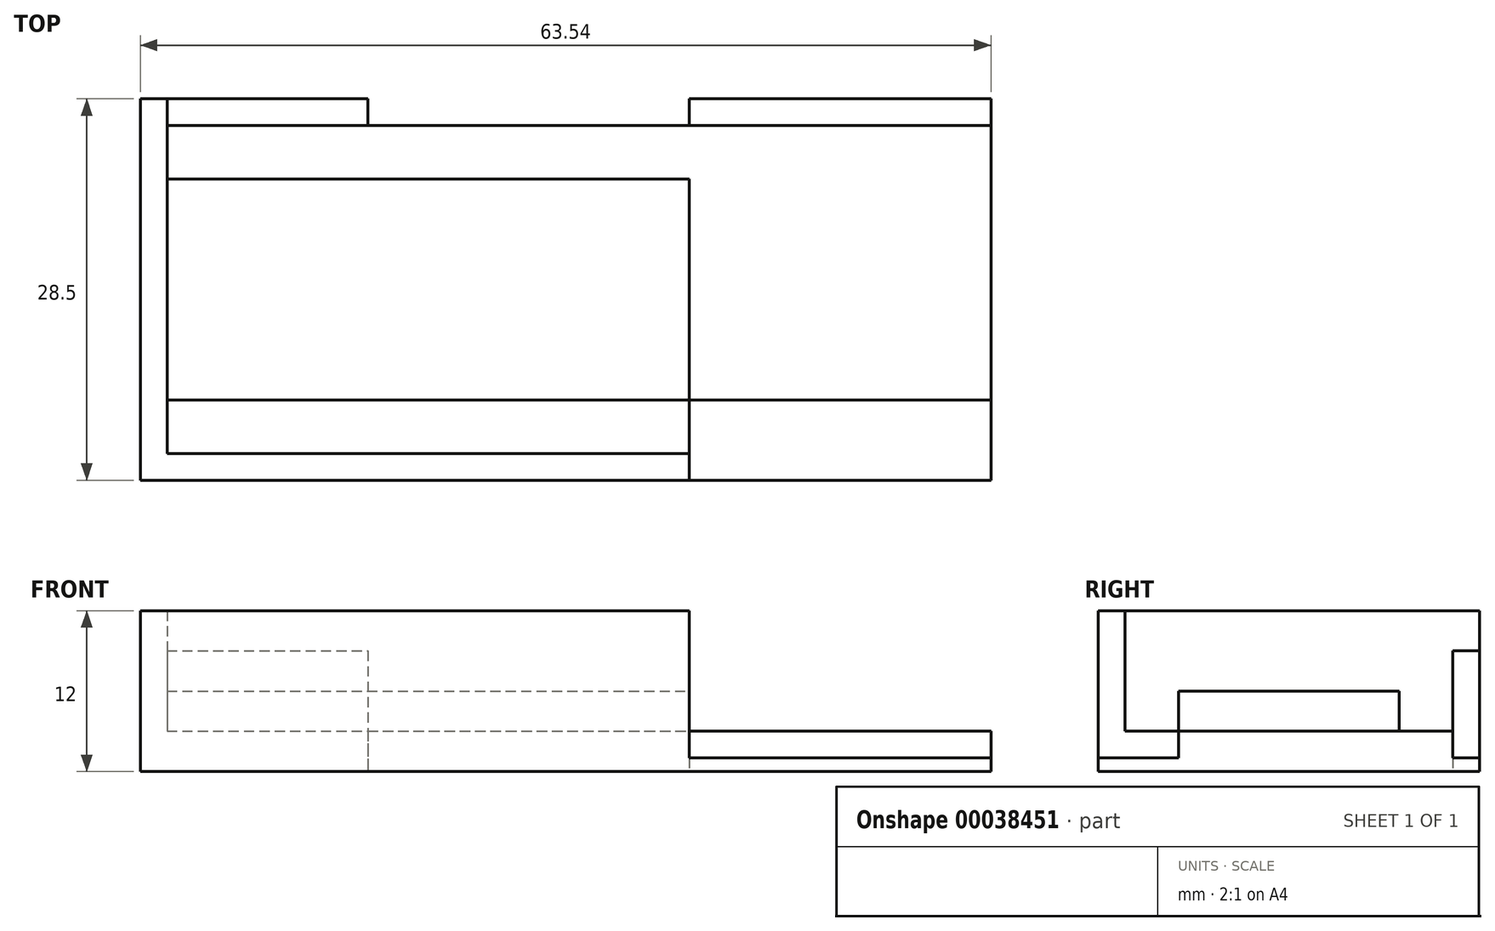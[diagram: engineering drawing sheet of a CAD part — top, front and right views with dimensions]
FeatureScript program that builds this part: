
annotation { "Feature Type Name" : "Feature", "Feature Type Description" : "" }
export const myFeature = defineFeature(function(context is Context, id is Id, definition is map)
    precondition{}
    {
        {
            var Q0;
            Q0=qCreatedBy(makeId("Top.planeOp"),FACE);
            var sketch = newSketch(context, id + "F0", { "sketchPlane" : qUnion([Q0])});
            skLineSegment(sketch, "E0.bottom", {"start": v(2, 26.5) * mm, "end": v(41, 26.5) * mm});
            skLineSegment(sketch, "E0.top", {"start": v(2, 2) * mm, "end": v(41, 2) * mm});
            skLineSegment(sketch, "E0.left", {"start": v(2, 26.5) * mm, "end": v(2, 2) * mm});
            skLineSegment(sketch, "E1.bottom", {"start": v(2, 22.5) * mm, "end": v(41, 22.5) * mm});
            skLineSegment(sketch, "E1.top", {"start": v(2, 6) * mm, "end": v(41, 6) * mm});
            skLineSegment(sketch, "E1.left", {"start": v(2, 22.5) * mm, "end": v(2, 6) * mm});
            skLineSegment(sketch, "E2.bottom", {"start": v(17, 26.5) * mm, "end": v(41, 26.5) * mm});
            skLineSegment(sketch, "E2.top", {"start": v(17, 28.5) * mm, "end": v(41, 28.5) * mm});
            skLineSegment(sketch, "E2.left", {"start": v(17, 26.5) * mm, "end": v(17, 28.5) * mm});
            skLineSegment(sketch, "E3.bottom", {"start": v(17, 28.5) * mm, "end": v(2, 28.5) * mm});
            skLineSegment(sketch, "E3.top", {"start": v(17, 26.5) * mm, "end": v(2, 26.5) * mm});
            skLineSegment(sketch, "E3.left", {"start": v(17, 28.5) * mm, "end": v(17, 26.5) * mm});
            skLineSegment(sketch, "E3.right", {"start": v(2, 28.5) * mm, "end": v(2, 26.5) * mm});
            skLineSegment(sketch, "E4.bottom", {"start": v(2, 28.5) * mm, "end": v(0, 28.5) * mm});
            skLineSegment(sketch, "E4.top", {"start": v(2, 2) * mm, "end": v(0, 2) * mm});
            skLineSegment(sketch, "E4.left", {"start": v(2, 28.5) * mm, "end": v(2, 2) * mm});
            skLineSegment(sketch, "E4.right", {"start": v(0, 28.5) * mm, "end": v(0, 2) * mm});
            skLineSegment(sketch, "E5.bottom", {"start": v(0, 2) * mm, "end": v(41, 2) * mm});
            skLineSegment(sketch, "E5.top", {"start": v(0, 0) * mm, "end": v(41, 0) * mm});
            skLineSegment(sketch, "E5.left", {"start": v(0, 2) * mm, "end": v(0, 0) * mm});
            skLineSegment(sketch, "E6.bottom", {"start": v(41, 26.5) * mm, "end": v(61, 26.5) * mm});
            skLineSegment(sketch, "E6.top", {"start": v(41, 6) * mm, "end": v(61, 6) * mm});
            skLineSegment(sketch, "E6.right", {"start": v(61, 26.5) * mm, "end": v(61, 6) * mm});
            skLineSegment(sketch, "E7", {"start": v(41, 28.5) * mm, "end": v(41, 0) * mm});
            skLineSegment(sketch, "E8.bottom", {"start": v(41, 28.5) * mm, "end": v(63.54, 28.5) * mm});
            skLineSegment(sketch, "E8.top", {"start": v(41, 0) * mm, "end": v(63.54, 0) * mm});
            skLineSegment(sketch, "E8.right", {"start": v(63.54, 28.5) * mm, "end": v(63.54, 0) * mm});
            skLineSegment(sketch, "E9", {"start": v(61, 6) * mm, "end": v(63.54, 6) * mm});
            skLineSegment(sketch, "E10", {"start": v(61, 26.5) * mm, "end": v(63.54, 26.5) * mm});
            skSolve(sketch);
        }
        {
            var Q0;
            {var subQ2=sQuery(id+"F0.wireOp",EDGE,"E6.bottom");Q0=makeQuery(id+"F0.imprint","IMPRINT",FACE,{"disambiguationData":[TD([[makeQuery(id+"F0.imprint","IMPRINT",EDGE,{"derivedFrom":subQ2}),-1.0]])]});}
            var Q1;
            {var subQ1=sQuery(id+"F0.wireOp",EDGE,"E1.bottom");Q1=makeQuery(id+"F0.imprint","IMPRINT",FACE,{"disambiguationData":[TD([[makeQuery(id+"F0.imprint","IMPRINT",EDGE,{"derivedFrom":subQ1}),1.0]])]});}
            var Q2;
            {var subQ0=sQuery(id+"F0.wireOp",EDGE,"E1.top");Q2=makeQuery(id+"F0.imprint","IMPRINT",FACE,{"disambiguationData":[TD([[makeQuery(id+"F0.imprint","IMPRINT",EDGE,{"derivedFrom":subQ0}),-1.0]])]});}
            var Q3;
            Q3=makeQuery(id+"F0.imprint","IMPRINT",FACE,{"disambiguationData":[TD([[makeQuery(id+"F0.imprint","IMPRINT",EDGE,{"derivedFrom":sQuery(id+"F0.wireOp",EDGE,"E6.right")}),1.0]])]});
            extrude(context, id + "F1", {"entities" : qUnion([Q0, Q1, Q2, Q3]), "depth" : 3 * mm});
        }
        {
            var Q0;
            {var subQ0=sQuery(id+"F0.wireOp",EDGE,"E1.bottom");Q0=makeQuery(id+"F0.imprint","IMPRINT",FACE,{"disambiguationData":[TD([[makeQuery(id+"F0.imprint","IMPRINT",EDGE,{"derivedFrom":subQ0}),-1.0]])]});}
            extrude(context, id + "F2", {"entities" : qUnion([Q0]), "depth" : 6 * mm});
        }
        {
            var Q0;
            {var subQ0=sQuery(id+"F0.wireOp",EDGE,"E3.bottom");Q0=makeQuery(id+"F0.imprint","IMPRINT",FACE,{"disambiguationData":[TD([[makeQuery(id+"F0.imprint","IMPRINT",EDGE,{"derivedFrom":subQ0}),1.0]])]});}
            extrude(context, id + "F3", {"entities" : qUnion([Q0]), "operationType" : NewBodyOperationType.ADD, "depth" : 9 * mm});
        }
        {
            var Q0;
            {var subQ0=sQuery(id+"F0.wireOp",EDGE,"E2.bottom");Q0=makeQuery(id+"F0.imprint","IMPRINT",FACE,{"disambiguationData":[TD([[makeQuery(id+"F0.imprint","IMPRINT",EDGE,{"derivedFrom":subQ0}),1.0]])]});}
            var Q1;
            {var subQ4=sQuery(id+"F0.wireOp",EDGE,"E4.bottom");Q1=makeQuery(id+"F0.imprint","IMPRINT",FACE,{"disambiguationData":[TD([[makeQuery(id+"F0.imprint","IMPRINT",EDGE,{"derivedFrom":subQ4}),1.0]])]});}
            var Q2;
            {var subQ1=sQuery(id+"F0.wireOp",EDGE,"E5.top");Q2=makeQuery(id+"F0.imprint","IMPRINT",FACE,{"disambiguationData":[TD([[makeQuery(id+"F0.imprint","IMPRINT",EDGE,{"derivedFrom":subQ1}),1.0]])]});}
            extrude(context, id + "F4", {"entities" : qUnion([Q0, Q1, Q2]), "depth" : 12 * mm});
        }
        {
            var Q0;
            {var subQ4=sQuery(id+"F0.wireOp",EDGE,"E6.bottom");Q0=makeQuery(id+"F0.imprint","IMPRINT",FACE,{"disambiguationData":[TD([[makeQuery(id+"F0.imprint","IMPRINT",EDGE,{"derivedFrom":subQ4}),1.0]])]});}
            var Q1;
            {var subQ3=sQuery(id+"F0.wireOp",EDGE,"E6.top");Q1=makeQuery(id+"F0.imprint","IMPRINT",FACE,{"disambiguationData":[TD([[makeQuery(id+"F0.imprint","IMPRINT",EDGE,{"derivedFrom":subQ3}),-1.0]])]});}
            extrude(context, id + "F5", {"entities" : qUnion([Q0, Q1]), "operationType" : NewBodyOperationType.ADD, "depth" : 1 * mm});
        }
    });
